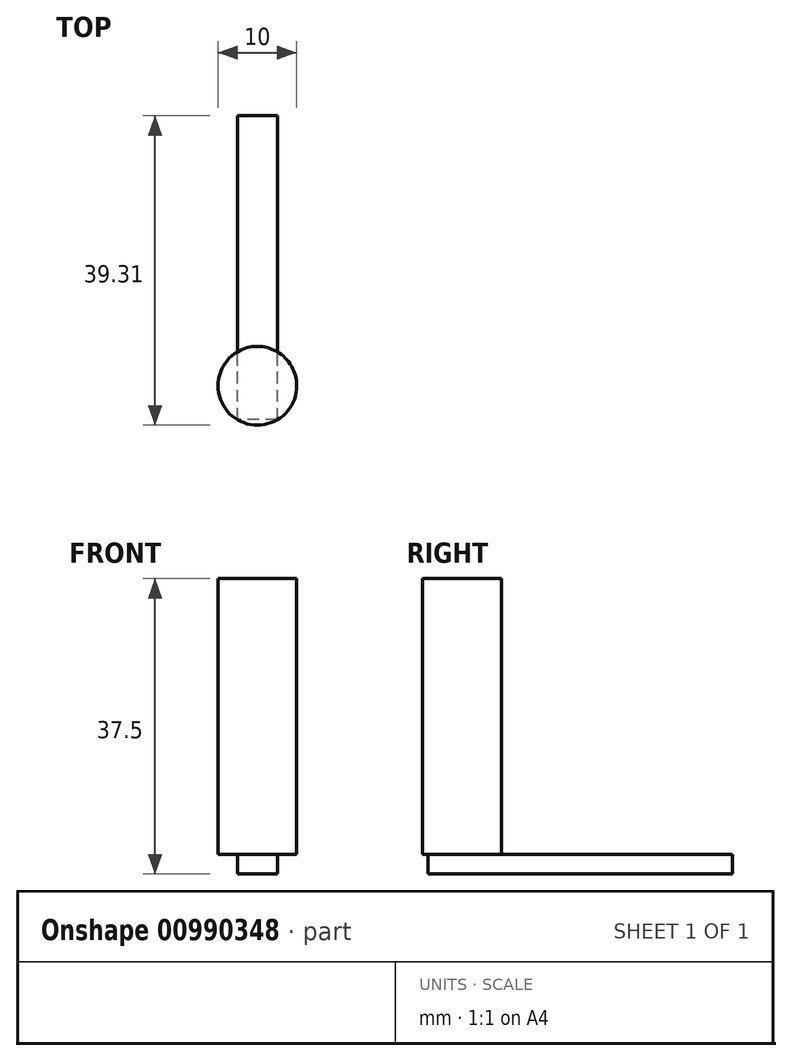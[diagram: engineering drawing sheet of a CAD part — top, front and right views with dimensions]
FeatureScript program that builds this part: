
annotation { "Feature Type Name" : "Feature", "Feature Type Description" : "" }
export const myFeature = defineFeature(function(context is Context, id is Id, definition is map)
    precondition{}
    {
        {
            var Q0;
            Q0=qCreatedBy(makeId("Top.planeOp"),FACE);
            var sketch = newSketch(context, id + "F0", { "sketchPlane" : qUnion([Q0])});
            skCircle(sketch, "E0", {"center": v(0, 0) * mm, "radius": 5 * mm});
            skSolve(sketch);
        }
        {
            var Q0;
            Q0 = qSketchRegion(id + "F0", true);
            extrude(context, id + "F1", {"entities" : qUnion([Q0]), "depth" : 35 * mm, "offsetDistance" : 25 * mm});
        }
        {
            var Q0;
            Q0=makeQuery(id+"F1.opExtrude","CAP_FACE",FACE,{"disambiguationData":[OSD([sQuery(id+"F0.wireOp",EDGE,"E0")])],"isStart":true});
            var sketch = newSketch(context, id + "F2", { "sketchPlane" : qUnion([Q0])});
            skLineSegment(sketch, "E1.bottom", {"start": v(2.53, 4.31) * mm, "end": v(-2.53, 4.31) * mm});
            skLineSegment(sketch, "E1.top", {"start": v(2.53, -14.31) * mm, "end": v(-2.53, -14.31) * mm});
            skLineSegment(sketch, "E1.left", {"start": v(2.53, 4.31) * mm, "end": v(2.53, -14.31) * mm});
            skLineSegment(sketch, "E1.right", {"start": v(-2.53, 4.31) * mm, "end": v(-2.53, -14.31) * mm});
            skPoint(sketch, "E1.middle", {"position": v(0, -5) * mm});
            skSolve(sketch);
        }
        {
            var Q0;
            Q0 = qSketchRegion(id + "F2", true);
            extrude(context, id + "F3", {"entities" : qUnion([Q0]), "operationType" : NewBodyOperationType.ADD, "depth" : 2.5 * mm, "offsetDistance" : 25 * mm});
        }
        {
            var Q0;
            Q0=makeQuery(id+"F3.opExtrude","SWEPT_FACE",FACE,{"disambiguationData":[OSD([sQuery(id+"F2.wireOp",EDGE,"E1.top")])]});
            extrude(context, id + "F4", {"entities" : qUnion([Q0]), "operationType" : NewBodyOperationType.ADD, "depth" : 20 * mm, "offsetDistance" : 25 * mm});
        }
    });
